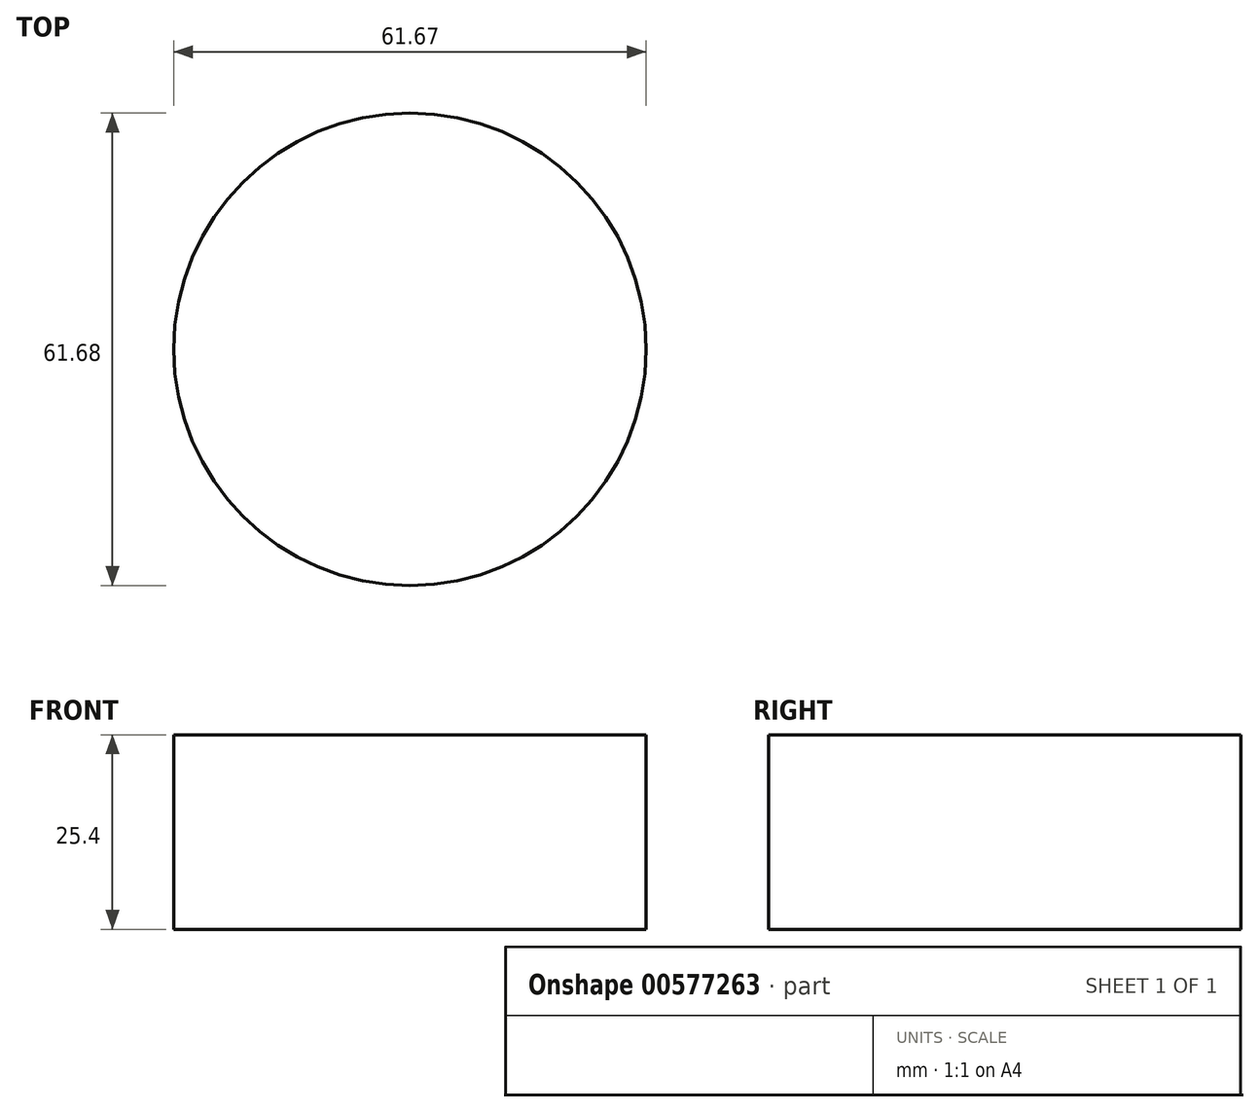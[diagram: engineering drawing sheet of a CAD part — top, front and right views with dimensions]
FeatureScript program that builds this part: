
annotation { "Feature Type Name" : "Feature", "Feature Type Description" : "" }
export const myFeature = defineFeature(function(context is Context, id is Id, definition is map)
    precondition{}
    {
        {
            var Q0;
            Q0=qCreatedBy(makeId("Top.planeOp"),FACE);
            var sketch = newSketch(context, id + "F0", { "sketchPlane" : qUnion([Q0])});
            skCircle(sketch, "E0", {"center": v(-109.7, 39.63) * mm, "radius": 30.84 * mm});
            skSolve(sketch);
        }
        {
            var Q0;
            Q0 = qSketchRegion(id + "F0", true);
            extrude(context, id + "F1", {"entities" : qUnion([Q0]), "depth" : 25.4 * mm, "offsetDistance" : 25.4 * mm});
        }
    });
